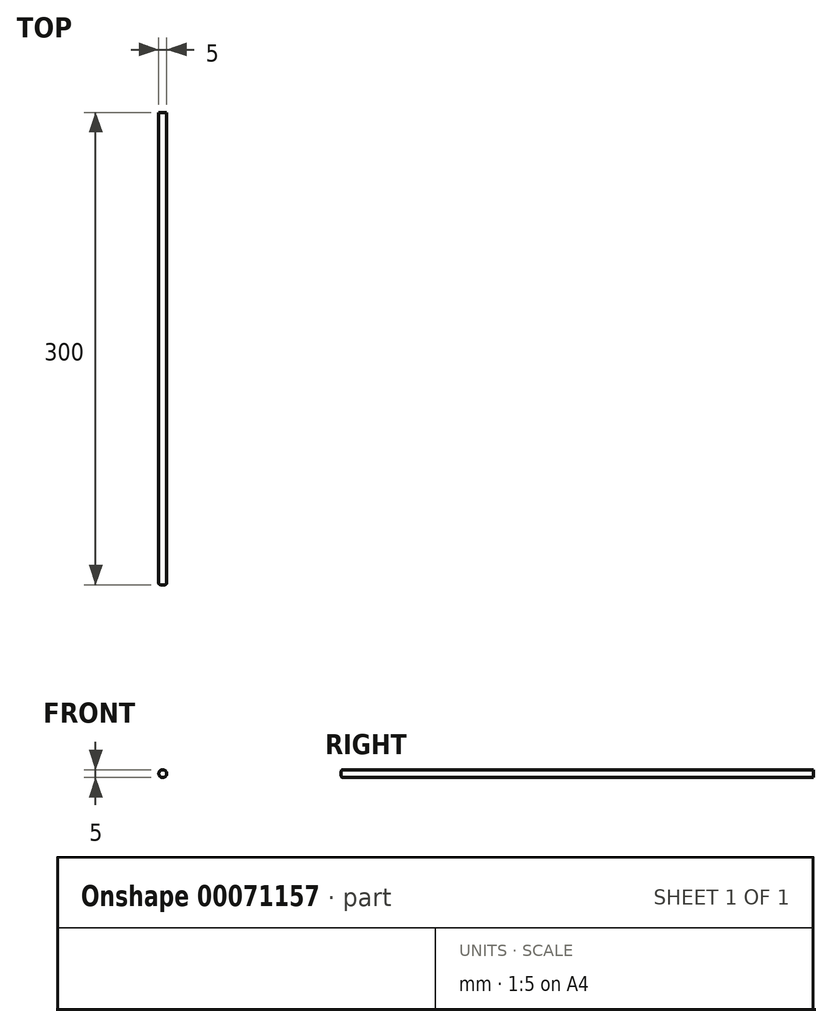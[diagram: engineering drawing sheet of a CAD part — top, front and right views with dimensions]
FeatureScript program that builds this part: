
annotation { "Feature Type Name" : "Feature", "Feature Type Description" : "" }
export const myFeature = defineFeature(function(context is Context, id is Id, definition is map)
    precondition{}
    {
        {
            var Q0;
            Q0=qCreatedBy(makeId("Front.planeOp"),FACE);
            var sketch = newSketch(context, id + "F0", { "sketchPlane" : qUnion([Q0])});
            skCircle(sketch, "E0", {"center": v(-95.52, 39.62) * mm, "radius": 2.5 * mm});
            skSolve(sketch);
        }
        {
            var Q0;
            Q0=makeQuery(id+"F0.imprint","IMPRINT",FACE,{"disambiguationData":[TD([[makeQuery(id+"F0.imprint","IMPRINT",EDGE,{"derivedFrom":sQuery(id+"F0.wireOp",EDGE,"E0")}),1.0]])]});
            extrude(context, id + "F1", {"entities" : qUnion([Q0]), "depth" : 300 * mm});
        }
        {
            var Q0;
            Q0=makeQuery(id+"F1.opExtrude","CAP_EDGE",EDGE,{"disambiguationData":[OSD([sQuery(id+"F0.wireOp",EDGE,"E0")])],"isStart":false});
            fillet(context, id + "F2", {"entities" : qUnion([Q0]), "radius" : 1 * mm, "tangentPropagation" : true, "allowEdgeOverflow" : false});
        }
    });
